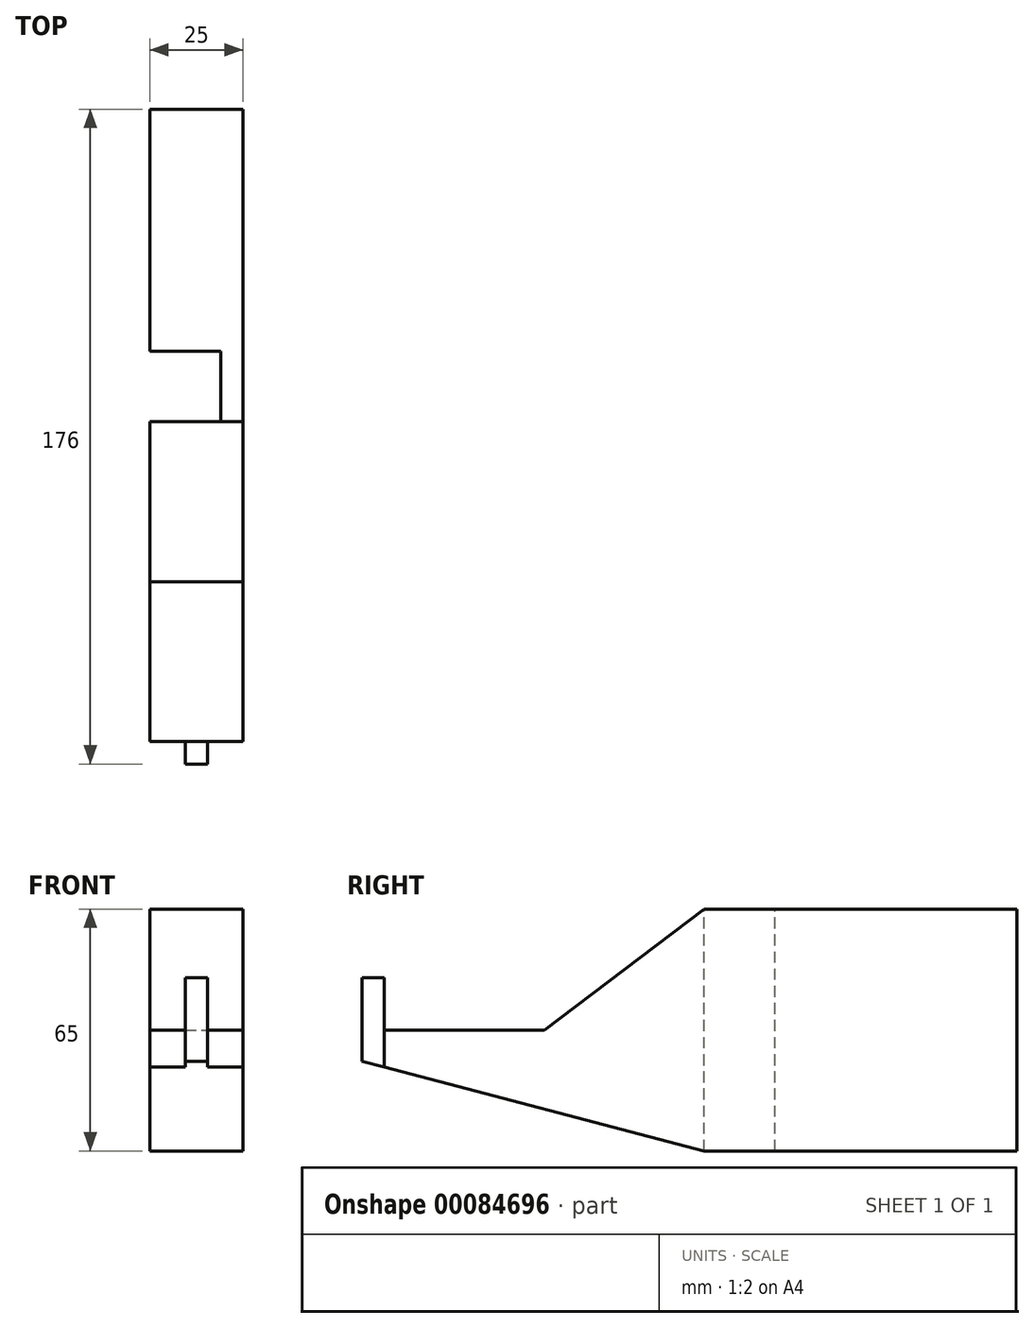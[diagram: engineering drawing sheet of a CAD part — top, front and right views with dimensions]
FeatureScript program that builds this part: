
annotation { "Feature Type Name" : "Feature", "Feature Type Description" : "" }
export const myFeature = defineFeature(function(context is Context, id is Id, definition is map)
    precondition{}
    {
        {
            var Q0;
            Q0=qCreatedBy(makeId("Right.planeOp"),FACE);
            var sketch = newSketch(context, id + "F0", { "sketchPlane" : qUnion([Q0])});
            skLineSegment(sketch, "E0.bottom", {"start": v(32.5, 32.5) * mm, "end": v(-32.5, 32.5) * mm});
            skLineSegment(sketch, "E0.top", {"start": v(32.5, -32.5) * mm, "end": v(-32.5, -32.5) * mm});
            skLineSegment(sketch, "E0.left", {"start": v(32.5, 32.5) * mm, "end": v(32.5, -32.5) * mm});
            skLineSegment(sketch, "E0.right", {"start": v(-32.5, 32.5) * mm, "end": v(-32.5, -32.5) * mm});
            skPoint(sketch, "E0.middle", {"position": v(0, 0) * mm});
            skSolve(sketch);
        }
        {
            var Q0;
            Q0=makeQuery(id+"F0.imprint","IMPRINT",FACE,{"disambiguationData":[TD([[makeQuery(id+"F0.imprint","IMPRINT",EDGE,{"derivedFrom":sQuery(id+"F0.wireOp",EDGE,"E0.bottom")}),1.0]])]});
            extrude(context, id + "F1", {"entities" : qUnion([Q0]), "depth" : 25 * mm});
        }
        {
            var Q0;
            Q0=makeQuery(id+"F1.opExtrude","SWEPT_FACE",FACE,{"disambiguationData":[OSD([sQuery(id+"F0.wireOp",EDGE,"E0.bottom")])]});
            var sketch = newSketch(context, id + "F2", { "sketchPlane" : qUnion([Q0])});
            skLineSegment(sketch, "E1.0", {"start": v(0, 32.5) * mm, "end": v(0, -32.5) * mm});
            skLineSegment(sketch, "E2.0", {"start": v(25, -32.5) * mm, "end": v(0, -32.5) * mm});
            skLineSegment(sketch, "E3.0", {"start": v(25, 32.5) * mm, "end": v(25, -32.5) * mm});
            skLineSegment(sketch, "E4.0", {"start": v(25, 32.5) * mm, "end": v(0, 32.5) * mm});
            skLineSegment(sketch, "E5", {"start": v(25, -32.5) * mm, "end": v(25, -51.5) * mm});
            skLineSegment(sketch, "E6", {"start": v(25, -51.5) * mm, "end": v(0, -51.5) * mm});
            skLineSegment(sketch, "E7", {"start": v(0, -51.5) * mm, "end": v(0, -137.5) * mm});
            skLineSegment(sketch, "E8", {"start": v(25, -51.5) * mm, "end": v(25, -137.5) * mm});
            skLineSegment(sketch, "E9", {"start": v(25, -137.5) * mm, "end": v(0, -137.5) * mm});
            skLineSegment(sketch, "E10", {"start": v(19, -51.5) * mm, "end": v(19, -32.5) * mm});
            skSolve(sketch);
        }
        {
            var Q0;
            {var subQ1=sQuery(id+"F2.wireOp",EDGE,"E7");Q0=makeQuery(id+"F2.imprint","IMPRINT",FACE,{"disambiguationData":[TD([[makeQuery(id+"F2.imprint","IMPRINT",EDGE,{"derivedFrom":subQ1}),1.0]])]});}
            var Q1;
            {var subQ0=sQuery(id+"F2.wireOp",EDGE,"E5");Q1=makeQuery(id+"F2.imprint","IMPRINT",FACE,{"disambiguationData":[TD([[makeQuery(id+"F2.imprint","IMPRINT",EDGE,{"derivedFrom":subQ0}),-1.0]])]});}
            var Q2;
            Q2=makeQuery(id+"F1.opExtrude","SWEPT_FACE",FACE,{"disambiguationData":[OSD([sQuery(id+"F0.wireOp",EDGE,"E0.top")])]});
            extrude(context, id + "F3", {"entities" : qUnion([Q0, Q1]), "operationType" : NewBodyOperationType.ADD, "endBound" : BoundingType.UP_TO_SURFACE, "oppositeDirection" : true, "endBoundEntityFace" : qUnion([Q2]), "depth" : 25 * mm});
        }
        {
            var Q0;
            Q0=makeQuery(id+"F3.boolean.opBoolean","MERGE",FACE,{"derivedFrom":[makeQuery(id+"F1.opExtrude","CAP_FACE",FACE,{"disambiguationData":[OSD([sQuery(id+"F0.wireOp",EDGE,"E0.bottom"),sQuery(id+"F0.wireOp",EDGE,"E0.top"),sQuery(id+"F0.wireOp",EDGE,"E0.left"),sQuery(id+"F0.wireOp",EDGE,"E0.right")])],"isStart":false}),makeQuery(id+"F3.opExtrude","SWEPT_FACE",FACE,{"disambiguationData":[OSD([sQuery(id+"F2.wireOp",EDGE,"E5"),sQuery(id+"F2.wireOp",EDGE,"E8")])]})]});
            var sketch = newSketch(context, id + "F4", { "sketchPlane" : qUnion([Q0])});
            skLineSegment(sketch, "E11.0", {"start": v(-137.5, -32.5) * mm, "end": v(-137.5, 32.5) * mm});
            skLineSegment(sketch, "E12.0", {"start": v(32.5, 32.5) * mm, "end": v(-137.5, 32.5) * mm});
            skLineSegment(sketch, "E13.0", {"start": v(32.5, -32.5) * mm, "end": v(-137.5, -32.5) * mm});
            skLineSegment(sketch, "E14.0", {"start": v(32.5, 32.5) * mm, "end": v(32.5, -32.5) * mm});
            skLineSegment(sketch, "E15.0", {"start": v(-51.5, -32.5) * mm, "end": v(-51.5, 32.5) * mm});
            skLineSegment(sketch, "E16", {"start": v(-51.5, 0) * mm, "end": v(-137.5, 0) * mm});
            skLineSegment(sketch, "E17", {"start": v(-137.5, -10) * mm, "end": v(-51.5, -32.5) * mm});
            skLineSegment(sketch, "E18", {"start": v(-51.5, 32.5) * mm, "end": v(-94.5, 0) * mm});
            skSolve(sketch);
        }
        {
            var Q0;
            {var subQ3=sQuery(id+"F4.wireOp",EDGE,"E17");Q0=makeQuery(id+"F4.imprint","IMPRINT",FACE,{"disambiguationData":[TD([[makeQuery(id+"F4.imprint","IMPRINT",EDGE,{"derivedFrom":subQ3}),-1.0]])]});}
            var Q1;
            {var subQ5=sQuery(id+"F4.wireOp",EDGE,"E18");Q1=makeQuery(id+"F4.imprint","IMPRINT",FACE,{"disambiguationData":[TD([[makeQuery(id+"F4.imprint","IMPRINT",EDGE,{"derivedFrom":subQ5}),-1.0]])]});}
            extrude(context, id + "F5", {"entities" : qUnion([Q0, Q1]), "operationType" : NewBodyOperationType.REMOVE, "oppositeDirection" : true, "depth" : 25 * mm});
        }
        {
            var Q0;
            Q0=makeQuery(id+"F5.boolean.opBoolean","COPY",FACE,{"derivedFrom":makeQuery(id+"F5.opExtrude","SWEPT_FACE",FACE,{"disambiguationData":[OSD([sQuery(id+"F4.wireOp",EDGE,"E16")])]})});
            var sketch = newSketch(context, id + "F6", { "sketchPlane" : qUnion([Q0])});
            skLineSegment(sketch, "E19.0", {"start": v(0, -137.5) * mm, "end": v(25, -137.5) * mm});
            skLineSegment(sketch, "E20.bottom", {"start": v(9.5, -143.5) * mm, "end": v(15.5, -143.5) * mm});
            skLineSegment(sketch, "E20.top", {"start": v(9.5, -137.5) * mm, "end": v(15.5, -137.5) * mm});
            skLineSegment(sketch, "E20.left", {"start": v(9.5, -143.5) * mm, "end": v(9.5, -137.5) * mm});
            skLineSegment(sketch, "E20.right", {"start": v(15.5, -143.5) * mm, "end": v(15.5, -137.5) * mm});
            skPoint(sketch, "E21", {"position": v(12.5, -137.5) * mm});
            skSolve(sketch);
        }
        {
            var Q0;
            Q0=makeQuery(id+"F6.imprint","IMPRINT",FACE,{"disambiguationData":[TD([[makeQuery(id+"F6.imprint","IMPRINT",EDGE,{"derivedFrom":sQuery(id+"F6.wireOp",EDGE,"E20.bottom")}),1.0]])]});
            var Q1;
            Q1=makeQuery(id+"F5.boolean.opBoolean","COPY",FACE,{"derivedFrom":makeQuery(id+"F5.opExtrude","SWEPT_FACE",FACE,{"disambiguationData":[OSD([sQuery(id+"F4.wireOp",EDGE,"E17")])]})});
            extrude(context, id + "F7", {"entities" : qUnion([Q0]), "operationType" : NewBodyOperationType.ADD, "depth" : 14 * mm, "hasSecondDirection" : true, "secondDirectionBound" : SecondDirectionBoundingType.UP_TO_SURFACE, "secondDirectionOppositeDirection" : true, "secondDirectionBoundEntityFace" : qUnion([Q1]), "secondDirectionDepth" : 25 * mm});
        }
    });
